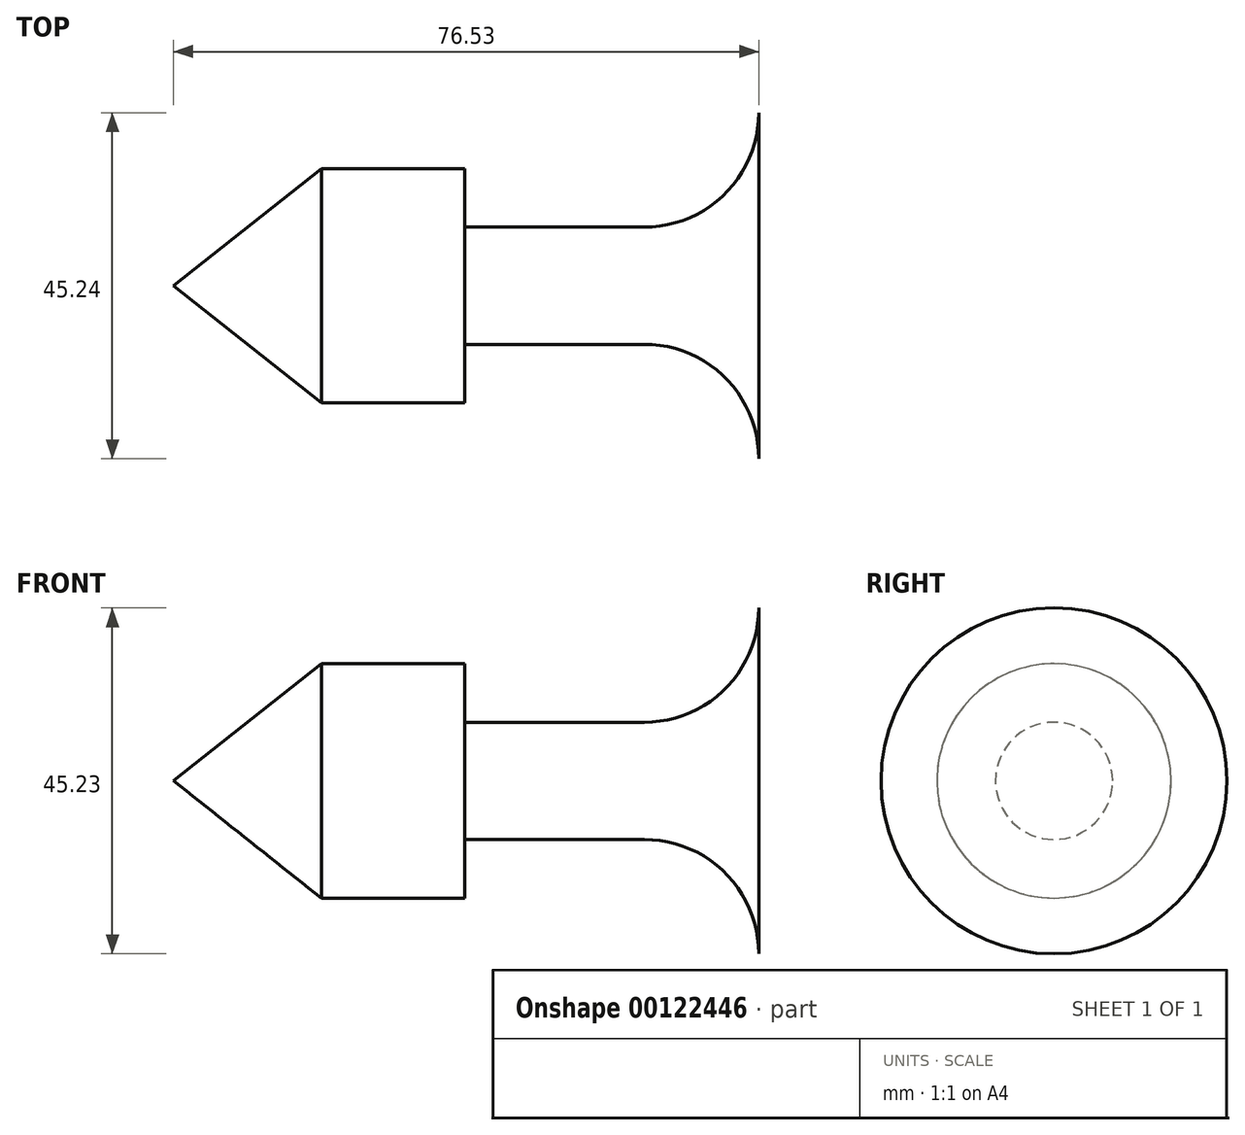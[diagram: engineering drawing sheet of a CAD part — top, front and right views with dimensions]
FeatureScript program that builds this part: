
annotation { "Feature Type Name" : "Feature", "Feature Type Description" : "" }
export const myFeature = defineFeature(function(context is Context, id is Id, definition is map)
    precondition{}
    {
        {
            var Q0;
            Q0=qCreatedBy(makeId("Front.planeOp"),FACE);
            var sketch = newSketch(context, id + "F0", { "sketchPlane" : qUnion([Q0])});
            skLineSegment(sketch, "E0.top", {"start": v(-46.7, -17.35) * mm, "end": v(29.83, -17.35) * mm});
            skLineSegment(sketch, "E1", {"start": v(-46.7, -17.35) * mm, "end": v(-27.38, -2.03) * mm});
            skLineSegment(sketch, "E2", {"start": v(-27.38, -2.03) * mm, "end": v(-8.64, -2.03) * mm});
            skLineSegment(sketch, "E3", {"start": v(-8.64, -2.03) * mm, "end": v(-8.64, -9.68) * mm});
            skLineSegment(sketch, "E4", {"start": v(-8.64, -9.68) * mm, "end": v(14.88, -9.68) * mm});
            skArc(sketch, "E5", {"start": v(14.88, -9.68) * mm, "mid": v(25.45, -5.3) * mm, "end": v(29.83, 5.27) * mm});
            skLineSegment(sketch, "E6", {"start": v(29.83, -17.35) * mm, "end": v(29.83, 5.27) * mm});
            skSolve(sketch);
        }
        {
            var Q0;
            Q0=makeQuery(id+"F0.imprint","IMPRINT",FACE,{"disambiguationData":[TD([[makeQuery(id+"F0.imprint","IMPRINT",EDGE,{"derivedFrom":sQuery(id+"F0.wireOp",EDGE,"E0.top")}),1.0]])]});
            var Q1;
            Q1=sQuery(id+"F0.wireOp",EDGE,"E0.top");
            revolve(context, id + "F1", {"entities" : qUnion([Q0]), "axis" : qUnion([Q1]), "revolveType" : RevolveType.FULL});
        }
    });
